FCSTD DOCUMENT  (FreeCAD 2024.113R14555 (Git shallow))
Label: ProtoKeyboardPiano-RT
License: All rights reserved
LicenseURL: https://en.wikipedia.org/wiki/All_rights_reserved
objects: Sketcher::SketchObject×1, PartDesign::Body×1
note: 3 computed .brp shape members not serialized (recipe doc carries the construction recipe); baked Part::Feature solids carry a one-line shape summary decoded from their .brp

FEATURE [Sketcher::SketchObject] Sketch
  ArcFitTolerance = 1e-06
  AttachmentSupport = -> [XY_Plane]
  ExternalBSplineMaxDegree = 5
  ExternalBSplineTolerance = 0.0001
  FullyConstrained = false
  InternalTolerance = 1e-06
  InvalidShape = false
  MakeInternals = false
  MapMode = 5
  Support = -> [XY_Plane]
  TreeRank = 11
  ValidateShape = false
  sketch-geometry (54):
    g0: LineSegment StartX=0 StartY=0 StartZ=0 EndX=161 EndY=0 EndZ=0
    g1: LineSegment StartX=161 StartY=0 StartZ=0 EndX=161 EndY=140 EndZ=0
    g2: LineSegment StartX=0 StartY=0 StartZ=0 EndX=23 EndY=0 EndZ=0
    g3: LineSegment StartX=23 StartY=0 StartZ=0 EndX=23 EndY=55 EndZ=0
    g4: LineSegment [constr] StartX=23 StartY=55 StartZ=0 EndX=0 EndY=55 EndZ=0
    g5: LineSegment StartX=0 StartY=55 StartZ=0 EndX=0 EndY=0 EndZ=0
    g6: LineSegment [constr] StartX=46 StartY=55 StartZ=0 EndX=69 EndY=55 EndZ=0
    g7: LineSegment StartX=69 StartY=55 StartZ=0 EndX=69 EndY=0 EndZ=0
    g8: LineSegment StartX=69 StartY=0 StartZ=0 EndX=46 EndY=0 EndZ=0
    g9: LineSegment StartX=46 StartY=0 StartZ=0 EndX=46 EndY=55 EndZ=0
    g10: LineSegment [constr] StartX=92 StartY=55 StartZ=0 EndX=115 EndY=55 EndZ=0
    g11: LineSegment StartX=115 StartY=55 StartZ=0 EndX=115 EndY=0 EndZ=0
    g12: LineSegment StartX=115 StartY=0 StartZ=0 EndX=92 EndY=0 EndZ=0
    g13: LineSegment StartX=92 StartY=0 StartZ=0 EndX=92 EndY=55 EndZ=0
    g14: LineSegment [constr] StartX=138 StartY=55 StartZ=0 EndX=161 EndY=55 EndZ=0
    g15: LineSegment StartX=161 StartY=55 StartZ=0 EndX=161 EndY=0 EndZ=0
    g16: LineSegment StartX=161 StartY=0 StartZ=0 EndX=138 EndY=0 EndZ=0
    g17: LineSegment StartX=138 StartY=0 StartZ=0 EndX=138 EndY=55 EndZ=0
    g18: LineSegment [constr] StartX=23 StartY=55 StartZ=0 EndX=46 EndY=55 EndZ=0
    g19: LineSegment [constr] StartX=69 StartY=55 StartZ=0 EndX=92 EndY=55 EndZ=0
    g20: LineSegment [constr] StartX=115 StartY=55 StartZ=0 EndX=138 EndY=55 EndZ=0
    g21: LineSegment StartX=12.7917 StartY=140 StartZ=0 EndX=27.7917 EndY=140 EndZ=0
    g22: LineSegment StartX=27.7917 StartY=140 StartZ=0 EndX=27.7917 EndY=55 EndZ=0
    g23: LineSegment StartX=27.7917 StartY=55 StartZ=0 EndX=12.7917 EndY=55 EndZ=0
    g24: LineSegment StartX=12.7917 StartY=55 StartZ=0 EndX=12.7917 EndY=140 EndZ=0
    g25: LineSegment StartX=41.2083 StartY=140 StartZ=0 EndX=56.2083 EndY=140 EndZ=0
    g26: LineSegment StartX=56.2083 StartY=140 StartZ=0 EndX=56.2083 EndY=55 EndZ=0
    g27: LineSegment StartX=56.2083 StartY=55 StartZ=0 EndX=41.2083 EndY=55 EndZ=0
    g28: LineSegment StartX=41.2083 StartY=55 StartZ=0 EndX=41.2083 EndY=140 EndZ=0
    g29: LineSegment StartX=79.0834 StartY=140 StartZ=0 EndX=94.0834 EndY=140 EndZ=0
    g30: LineSegment StartX=94.0834 StartY=140 StartZ=0 EndX=94.0834 EndY=55 EndZ=0
    g31: LineSegment StartX=79.0834 StartY=55 StartZ=0 EndX=79.0834 EndY=140 EndZ=0
    g32: LineSegment StartX=107.5 StartY=140 StartZ=0 EndX=122.5 EndY=140 EndZ=0
    g33: LineSegment StartX=122.5 StartY=140 StartZ=0 EndX=122.5 EndY=55 EndZ=0
    g34: LineSegment StartX=122.5 StartY=55 StartZ=0 EndX=107.5 EndY=55 EndZ=0
    g35: LineSegment StartX=107.5 StartY=55 StartZ=0 EndX=107.5 EndY=140 EndZ=0
    g36: LineSegment StartX=135.917 StartY=140 StartZ=0 EndX=150.917 EndY=140 EndZ=0
    g37: LineSegment StartX=150.917 StartY=140 StartZ=0 EndX=150.917 EndY=55 EndZ=0
    g38: LineSegment StartX=150.917 StartY=55 StartZ=0 EndX=135.917 EndY=55 EndZ=0
    g39: LineSegment StartX=135.917 StartY=55 StartZ=0 EndX=135.917 EndY=140 EndZ=0
    g40: LineSegment [constr] StartX=0 StartY=140 StartZ=0 EndX=12.7917 EndY=140 EndZ=0
    g41: LineSegment [constr] StartX=27.7917 StartY=140 StartZ=0 EndX=41.2083 EndY=140 EndZ=0
    g42: LineSegment [constr] StartX=94.0834 StartY=140 StartZ=0 EndX=107.5 EndY=140 EndZ=0
    g43: LineSegment [constr] StartX=122.5 StartY=140 StartZ=0 EndX=135.917 EndY=140 EndZ=0
    g44: LineSegment [constr] StartX=150.917 StartY=140 StartZ=0 EndX=161 EndY=140 EndZ=0
    g45: GeomPoint [constr] X=20.2917 Y=55 Z=0
    g46: GeomPoint [constr] X=48.7083 Y=55 Z=0
    g47: LineSegment [constr] StartX=34.5 StartY=140 StartZ=0 EndX=34.5 EndY=0 EndZ=0
    g48: LineSegment [constr] StartX=56.2083 StartY=140 StartZ=0 EndX=69 EndY=140 EndZ=0
    g49: LineSegment [constr] StartX=79.0834 StartY=140 StartZ=0 EndX=69 EndY=140 EndZ=0
    g50: LineSegment [constr] StartX=69 StartY=140 StartZ=0 EndX=69 EndY=55 EndZ=0
    g51: LineSegment StartX=0 StartY=140 StartZ=0 EndX=0 EndY=55 EndZ=0
    g52: GeomPoint [constr] X=87.3703 Y=55 Z=0
    g53: GeomPoint [constr] X=143.417 Y=55 Z=0
  constraints (147):
    c: Coincident(g0,g1)
    c: Horizontal(g0)
    c: Vertical(g1)
    c: Coincident(g0,g-1)
    c: Coincident(g2,g3)
    c: Coincident(g3,g4)
    c: Coincident(g4,g5)
    c: Coincident(g5,g2)
    c: Horizontal(g2)
    c: Horizontal(g4)
    c: Vertical(g3)
    c: Vertical(g5)
    c: Coincident(g2,g0)
    c: Coincident(g6,g7)
    c: Coincident(g7,g8)
    c: Coincident(g8,g9)
    c: Coincident(g9,g6)
    c: Horizontal(g6)
    c: Horizontal(g8)
    c: Vertical(g7)
    c: Vertical(g9)
    c: PointOnObject(g7,g0)
    c: Coincident(g10,g11)
    c: Coincident(g11,g12)
    c: Coincident(g12,g13)
    c: Coincident(g13,g10)
    c: Horizontal(g10)
    c: Horizontal(g12)
    c: Vertical(g11)
    c: Vertical(g13)
    c: PointOnObject(g11,g0)
    c: Coincident(g14,g15)
    c: Coincident(g15,g16)
    c: Coincident(g16,g17)
    c: Coincident(g17,g14)
    c: Horizontal(g14)
    c: Horizontal(g16)
    c: Vertical(g15)
    c: Vertical(g17)
    c: Coincident(g15,g0)
    c: Coincident(g18,g3)
    c: Coincident(g18,g6)
    c: Horizontal(g18)
    c: Coincident(g19,g6)
    c: Coincident(g19,g10)
    c: Horizontal(g19)
    c: Coincident(g20,g10)
    c: Coincident(g20,g14)
    c: Horizontal(g20)
    c: Equal(g4,g18)
    c: Equal(g18,g6)
    c: Equal(g6,g19)
    c: Equal(g19,g10)
    c: Equal(g10,g20)
    c: DistanceX(g16,g0) = 23
    c: DistanceX(g0,g0) = 161
    c: Coincident(g21,g22)
    c: Coincident(g22,g23)
    c: Coincident(g23,g24)
    c: Coincident(g24,g21)
    c: Horizontal(g21)
    c: Horizontal(g23)
    c: Vertical(g22)
    c: Vertical(g24)
    c: PointOnObject(g22,g18)
    c: Coincident(g25,g26)
    c: Coincident(g26,g27)
    c: Coincident(g27,g28)
    c: Coincident(g28,g25)
    c: Horizontal(g25)
    c: Horizontal(g27)
    c: Vertical(g26)
    c: Vertical(g28)
    c: PointOnObject(g26,g6)
    c: Coincident(g29,g30)
    c: Coincident(g31,g29)
    c: Horizontal(g29)
    c: Vertical(g30)
    c: Vertical(g31)
    c: Coincident(g32,g33)
    c: Coincident(g33,g34)
    c: Coincident(g34,g35)
    c: Coincident(g35,g32)
    c: Horizontal(g32)
    c: Horizontal(g34)
    c: Vertical(g33)
    c: Vertical(g35)
    c: Coincident(g36,g37)
    c: Coincident(g37,g38)
    c: Coincident(g38,g39)
    c: Coincident(g39,g36)
    c: Horizontal(g36)
    c: Horizontal(g38)
    c: Vertical(g37)
    c: Vertical(g39)
    c: Equal(g23,g27)
    c: Coincident(g40,g21)
    c: Horizontal(g40)
    c: Coincident(g41,g21)
    c: Coincident(g41,g25)
    c: Horizontal(g41)
    c: Coincident(g42,g29)
    c: Coincident(g42,g32)
    c: Horizontal(g42)
    c: Coincident(g43,g32)
    c: Coincident(g43,g36)
    c: Horizontal(g43)
    c: Coincident(g44,g36)
    c: Coincident(g44,g1)
    c: Horizontal(g44)
    c: DistanceY(g1,g1) = 140
    c: DistanceY(g0,g15) = 55
    c: DistanceX(g23,g23) = 15
    c: Symmetric(g23,g22,g45)
    c: Symmetric(g27,g26,g46)
    c: DistanceX(g5,g45) = 20.2917
    c: Equal(g38,g34)
    c: Equal(g14,g20)
    c: Symmetric(g34,g33,g11)
    c: DistanceX(g36,g36) = 15
    c: PointOnObject(g47,g41)
    c: Symmetric(g2,g8,g47)
    c: Symmetric(g22,g27,g47)
    c: Coincident(g48,g25)
    c: Horizontal(g48)
    c: Coincident(g49,g29)
    c: Coincident(g49,g48)
    c: Horizontal(g49)
    c: Coincident(g50,g48)
    c: Coincident(g50,g7)
    c: Vertical(g50)
    c: Symmetric(g30,g38,g11)
    c: Equal(g29,g36)
    c: DistanceX(g25,g25) = 15
    c: Coincident(g51,g40)
    c: Coincident(g51,g5)
    c: Vertical(g51)
    c: Equal(g41,g42)
    c: DistanceX(g43,g43) = 13.4166
    c: PointOnObject(g31,g19)
    c: PointOnObject(g37,g14)
    c: DistanceX(g5,g46) = 48.7083
    c: PointOnObject(g52,g19)
    c: PointOnObject(g53,g38)
    c: DistanceX(g5,g11) = 115
    c: DistanceX(g5,g52) = 87.3703
    c: DistanceX(g5,g53) = 143.417
FEATURE [PartDesign::Body] Body
  AutoGroupSolids = false
  ClaimAllChildren = false
  ExportMode = 0
  Group = -> [Sketch]
  InvalidShape = false
  Origin = -> Origin
  TreeRank = 10
  ValidateShape = false
  _ExportChildren = -> [Sketch]
  _GroupVersion = 1
